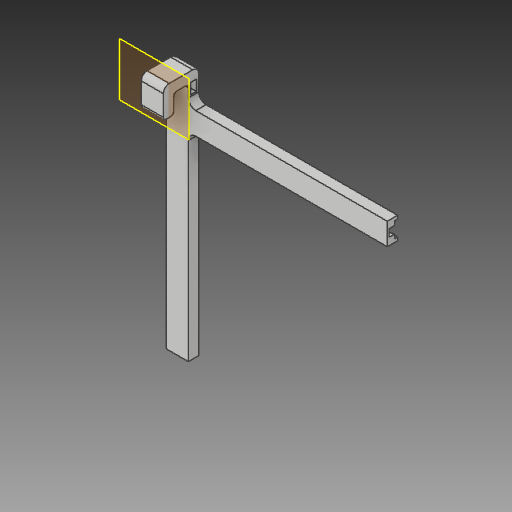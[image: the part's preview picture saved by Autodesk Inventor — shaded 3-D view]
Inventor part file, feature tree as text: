
AUTODESK INVENTOR PART (.ipt)
format: ipt  version: 2017 (Build 210142000, 142)  size: 167,936 bytes
history: native  units: in
note: dims shown in document units (in); Inventor stores cm internally (conversion verified against a paired STEP export)
features: sketch x4, other x3, plane x1
ambient origin geometry x8: Origin, YZ Plane, XZ Plane, XY Plane, X Axis, Y Axis, Z Axis, Center Point
bodies: Solid1 (feature_tree)
feature tree (8):
  other  "Top Clip.ipt"
  other  "Solid1::Top Clip.ipt"
  other  "TaggingFeature1"
  sketch  "Sketch1"  dims[d0=0.3937in]
  sketch  "Sketch2"
  sketch  "Sketch6"
  sketch  "Sketch7"
  plane  "Work Plane1"
